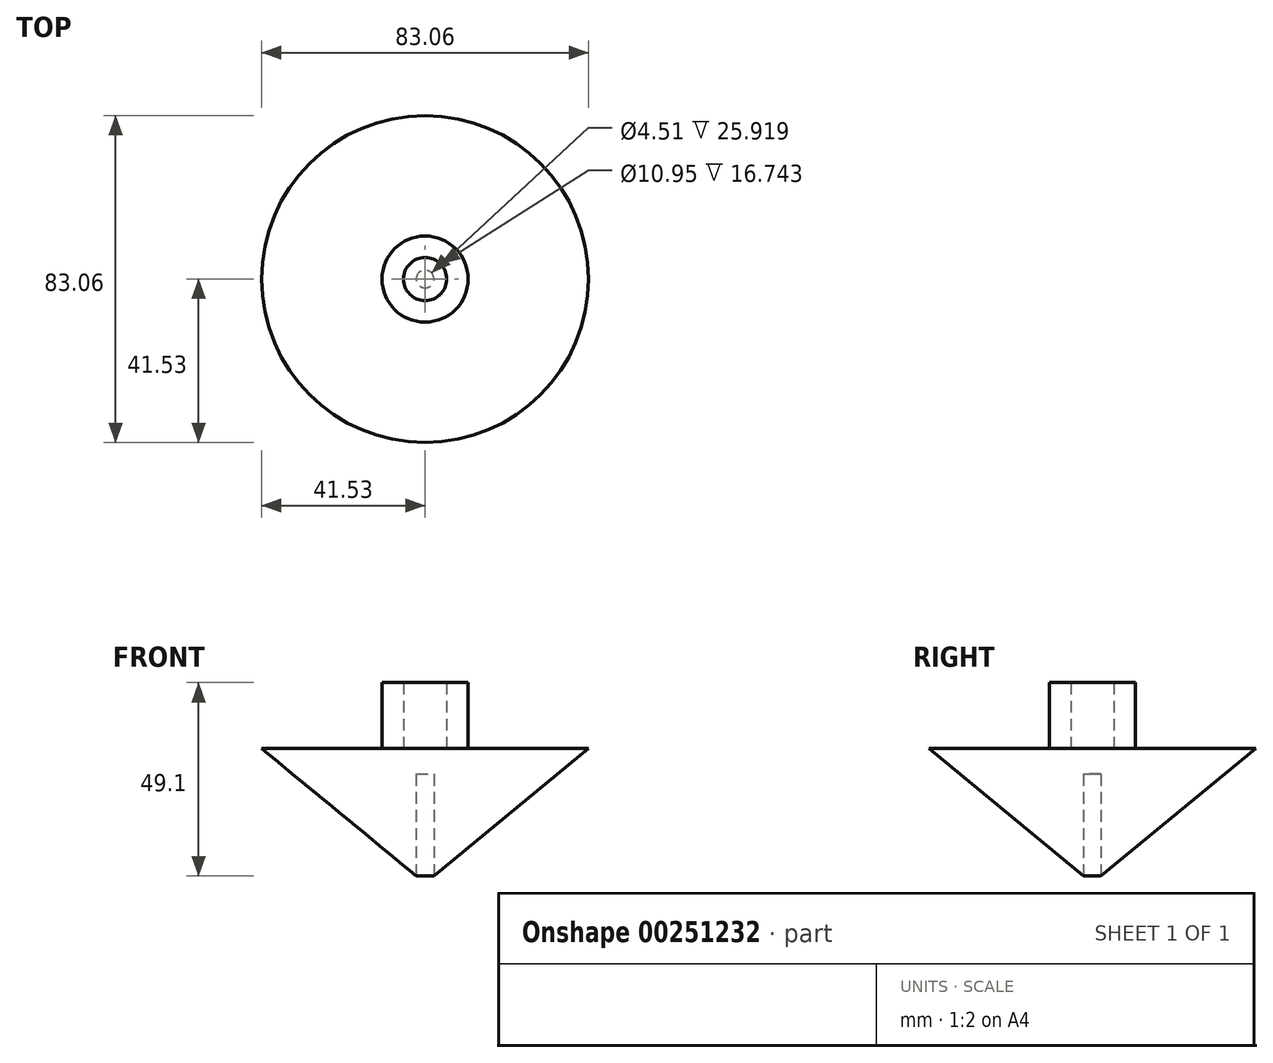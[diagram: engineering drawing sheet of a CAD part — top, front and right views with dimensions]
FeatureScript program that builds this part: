
annotation { "Feature Type Name" : "Feature", "Feature Type Description" : "" }
export const myFeature = defineFeature(function(context is Context, id is Id, definition is map)
    precondition{}
    {
        {
            var Q0;
            Q0=qCreatedBy(makeId("Front.planeOp"),FACE);
            var sketch = newSketch(context, id + "F0", { "sketchPlane" : qUnion([Q0])});
            skLineSegment(sketch, "E0", {"start": v(2.25, 0) * mm, "end": v(2.25, 25.92) * mm});
            skLineSegment(sketch, "E1", {"start": v(2.25, 25.92) * mm, "end": v(0, 25.92) * mm});
            skLineSegment(sketch, "E2", {"start": v(0, 25.92) * mm, "end": v(0, 32.36) * mm});
            skLineSegment(sketch, "E3", {"start": v(0, 32.36) * mm, "end": v(5.47, 32.36) * mm});
            skLineSegment(sketch, "E4", {"start": v(5.47, 32.36) * mm, "end": v(5.47, 49.1) * mm});
            skLineSegment(sketch, "E5", {"start": v(5.47, 49.1) * mm, "end": v(10.95, 49.1) * mm});
            skLineSegment(sketch, "E6", {"start": v(10.95, 49.1) * mm, "end": v(10.95, 32.36) * mm});
            skLineSegment(sketch, "E7", {"start": v(10.95, 32.36) * mm, "end": v(41.53, 32.36) * mm});
            skLineSegment(sketch, "E8", {"start": v(41.53, 32.36) * mm, "end": v(2.25, 0) * mm});
            skSolve(sketch);
        }
        {
            var Q0;
            Q0=makeQuery(id+"F0.imprint","IMPRINT",FACE,{"disambiguationData":[TD([[makeQuery(id+"F0.imprint","IMPRINT",EDGE,{"derivedFrom":sQuery(id+"F0.wireOp",EDGE,"E0")}),-1.0]])]});
            var Q1;
            Q1=sQuery(id+"F0.wireOp",EDGE,"E2");
            revolve(context, id + "F1", {"entities" : qUnion([Q0]), "axis" : qUnion([Q1]), "revolveType" : RevolveType.FULL});
        }
    });
